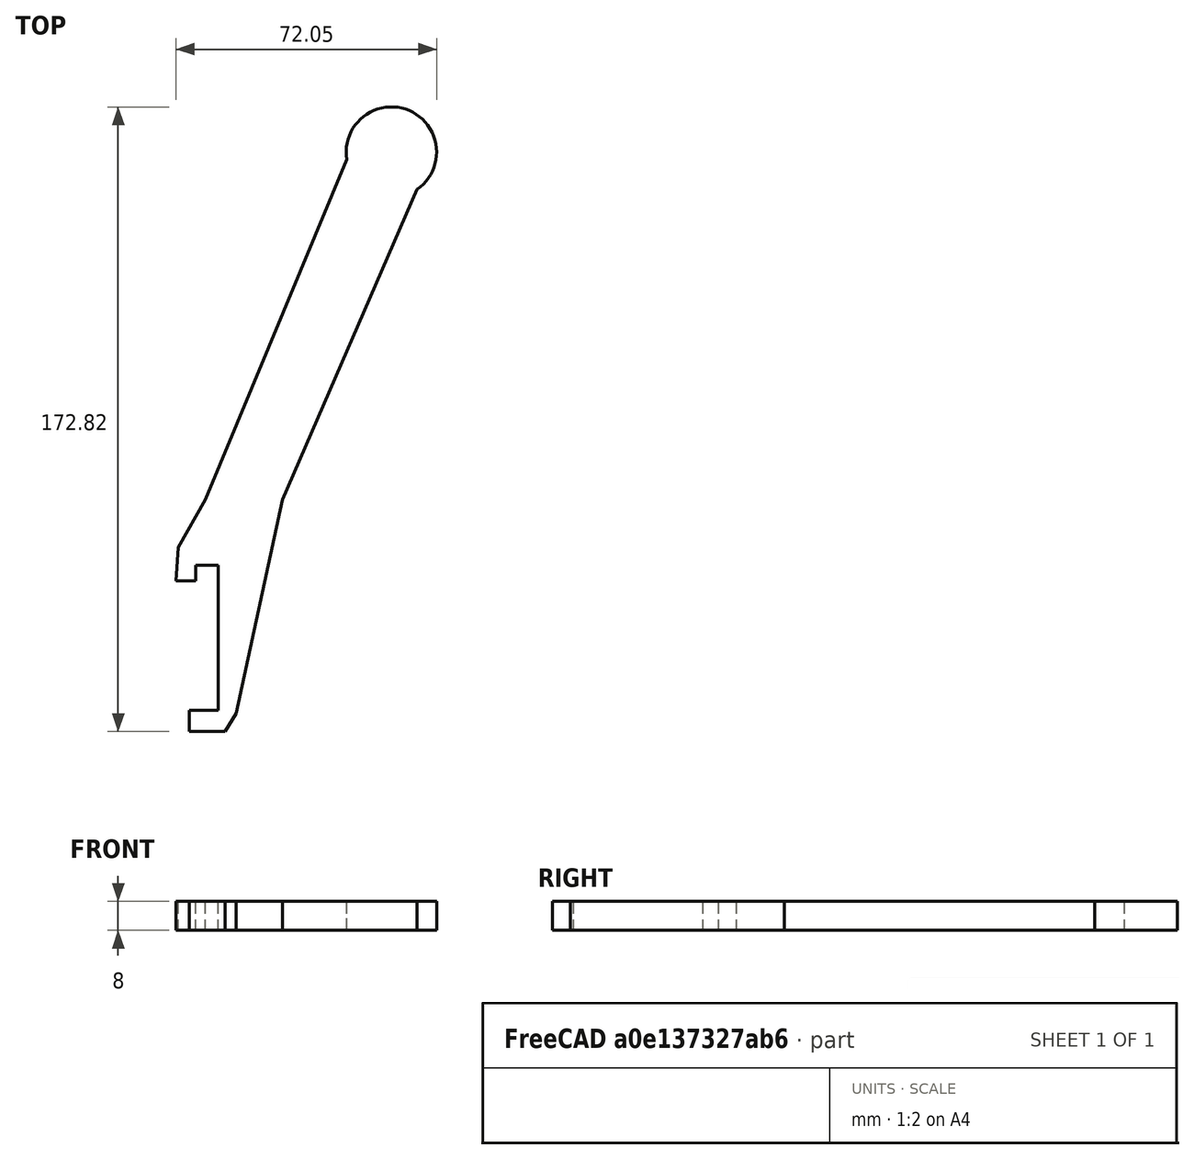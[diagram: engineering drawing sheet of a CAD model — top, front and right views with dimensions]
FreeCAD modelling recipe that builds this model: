
FCSTD DOCUMENT  (FreeCAD 0.16R6705 (Git))
Label: holder
License: All rights reserved
LicenseURL: http://it.wikipedia.org/wiki/<copyright redacted>
objects: Sketcher::SketchObject×1, PartDesign::Pad×1
note: 3 computed .brp shape members not serialized (recipe doc carries the construction recipe); baked Part::Feature solids carry a one-line shape summary decoded from their .brp

FEATURE [Sketcher::SketchObject] Sketch015
  sketch-geometry (15):
    g0: LineSegment StartX=0 StartY=-40.1 StartZ=0 EndX=0 EndY=0 EndZ=0
    g1: LineSegment StartX=17.8486 StartY=18.1391 StartZ=0 EndX=55 EndY=104 EndZ=0
    g2: LineSegment StartX=-8 StartY=-40.1 StartZ=0 EndX=0 EndY=-40.1 EndZ=0
    g3: LineSegment StartX=-3.48139 StartY=18.1153 StartZ=0 EndX=-11 EndY=5 EndZ=0
    g4: ArcOfCircle CenterX=47.9468 CenterY=114.32 CenterZ=0 NormalX=0 NormalY=0 NormalZ=1 Radius=12.5 StartAngle=5.31192 EndAngle=9.58683
    g5: LineSegment StartX=-8 StartY=-40.1 StartZ=0 EndX=-8 EndY=-46 EndZ=0
    g6: LineSegment StartX=-8 StartY=-46 StartZ=0 EndX=2 EndY=-46 EndZ=0
    g7: LineSegment StartX=0 StartY=0 StartZ=0 EndX=-6.2 EndY=0 EndZ=0
    g8: LineSegment StartX=-3.48139 StartY=18.1153 StartZ=0 EndX=35.6106 EndY=112.303 EndZ=0
    g9: LineSegment StartX=5 StartY=-41 StartZ=0 EndX=17.8486 EndY=18.1391 EndZ=0
    g10: LineSegment StartX=-6.2 StartY=0 StartZ=0 EndX=-6.2 EndY=-4.3 EndZ=0
    g11: LineSegment StartX=-8 StartY=-40.1 StartZ=0 EndX=0 EndY=-40.1 EndZ=0
    g12: LineSegment StartX=2 StartY=-46 StartZ=0 EndX=5 EndY=-41 EndZ=0
    g13: LineSegment StartX=-11 StartY=5 StartZ=0 EndX=-11.6 EndY=-4.3 EndZ=0
    g14: LineSegment StartX=-11.6 StartY=-4.3 StartZ=0 EndX=-6.2 EndY=-4.3 EndZ=0
  constraints (2):
    c: PointOnObject(g10,g14)
    c: Coincident(g2,g11)
FEATURE [PartDesign::Pad] Pad
  Length = 8
  Length2 = 100
  Sketch = -> Sketch015
  Type = 0
